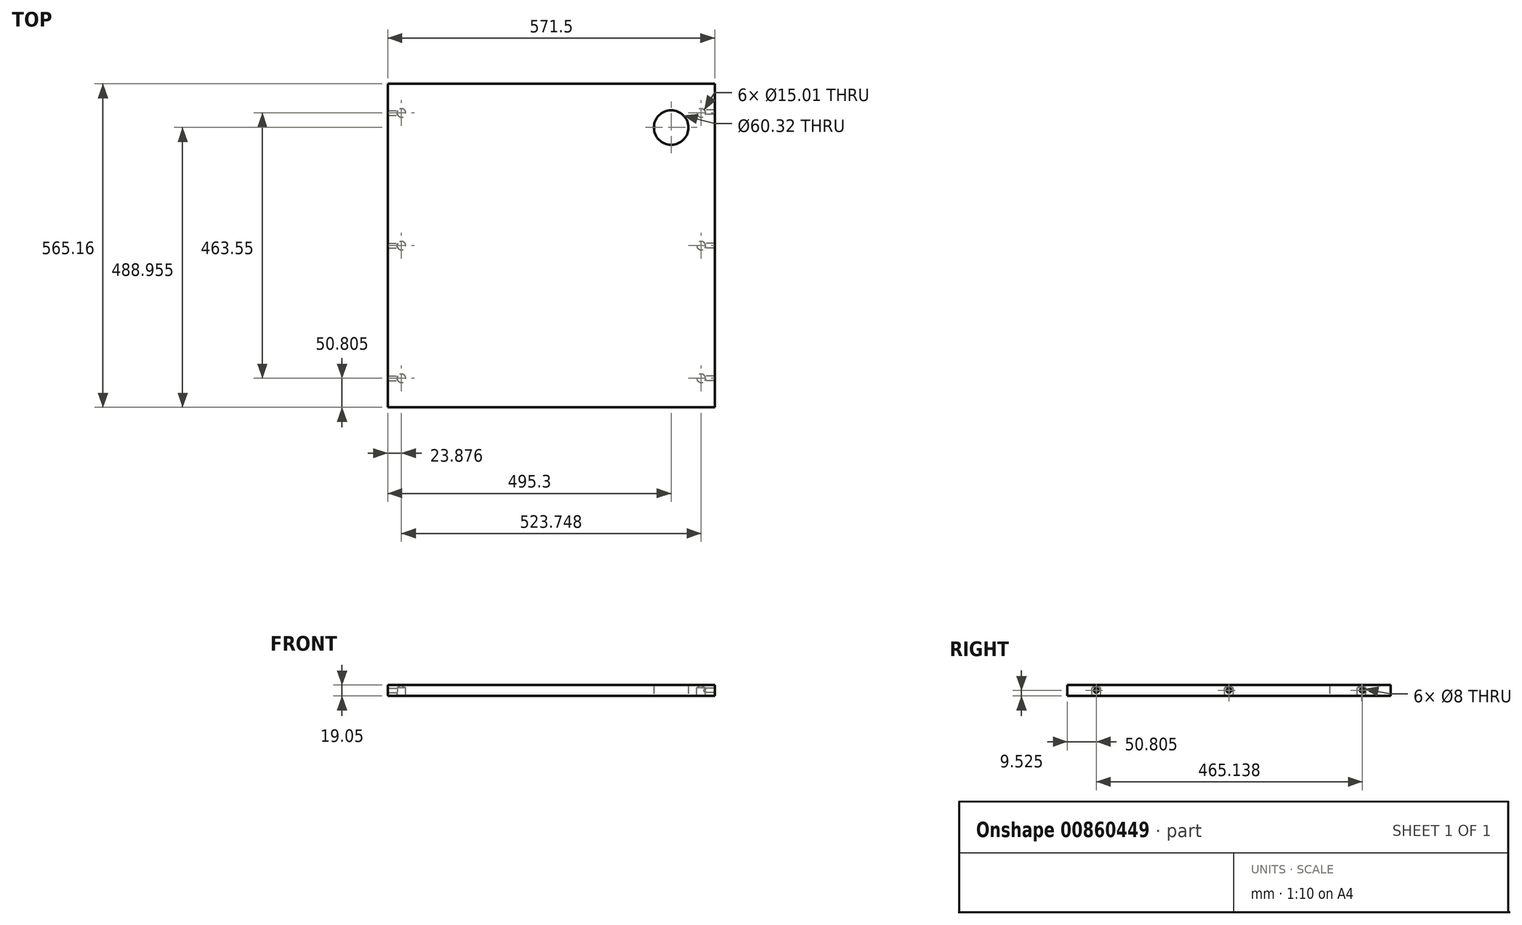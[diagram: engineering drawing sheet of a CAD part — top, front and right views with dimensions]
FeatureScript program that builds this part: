
annotation { "Feature Type Name" : "Feature", "Feature Type Description" : "" }
export const myFeature = defineFeature(function(context is Context, id is Id, definition is map)
    precondition{}
    {
        {
            var Q0;
            Q0=qCreatedBy(makeId("Top.planeOp"),FACE);
            var sketch = newSketch(context, id + "F0", { "sketchPlane" : qUnion([Q0])});
            skLineSegment(sketch, "E0.bottom", {"start": v(285.75, 282.58) * mm, "end": v(-285.75, 282.58) * mm});
            skLineSegment(sketch, "E0.top", {"start": v(285.75, -282.57) * mm, "end": v(-285.75, -282.58) * mm});
            skLineSegment(sketch, "E0.left", {"start": v(285.75, 282.58) * mm, "end": v(285.75, -282.58) * mm});
            skLineSegment(sketch, "E0.right", {"start": v(-285.75, 282.58) * mm, "end": v(-285.75, -282.58) * mm});
            skPoint(sketch, "E0.middle", {"position": v(0, 0) * mm});
            skCircle(sketch, "E1", {"center": v(209.55, 206.38) * mm, "radius": 30.16 * mm});
            skLineSegment(sketch, "E2", {"start": v(209.55, 206.38) * mm, "end": v(285.75, 206.38) * mm});
            skLineSegment(sketch, "E3", {"start": v(209.55, 206.38) * mm, "end": v(209.55, 282.58) * mm});
            skSolve(sketch);
        }
        {
            var Q0;
            Q0=makeQuery(id+"F0.imprint","IMPRINT",FACE,{"disambiguationData":[TD([[makeQuery(id+"F0.imprint","IMPRINT",EDGE,{"derivedFrom":sQuery(id+"F0.wireOp",EDGE,"E0.top")}),-1.0]])]});
            var Q1;
            {var subQ1=sQuery(id+"F0.wireOp",EDGE,"E0.left");var subQ7=sQuery(id+"F0.wireOp",EDGE,"E0.bottom");var subQ8=makeQuery(id+"F0.imprint","INTERSECT",VERTEX,{"derivedFrom":[subQ7,subQ1]});Q1=makeQuery(id+"F0.imprint","IMPRINT",FACE,{"disambiguationData":[TD([[makeQuery(id+"F0.imprint","IMPRINT",EDGE,{"disambiguationData":[TD([[subQ8,-1.0]])],"derivedFrom":subQ7}),1.0]])]});}
            extrude(context, id + "F1", {"entities" : qUnion([Q0, Q1]), "depth" : 19.05 * mm, "offsetDistance" : 25.4 * mm});
        }
        {
            var Q0;
            Q0=makeQuery(id+"F1.opExtrude","CAP_FACE",FACE,{"disambiguationData":[OSD([sQuery(id+"F0.wireOp",EDGE,"E0.bottom"),sQuery(id+"F0.wireOp",EDGE,"E0.top"),sQuery(id+"F0.wireOp",EDGE,"E0.left"),sQuery(id+"F0.wireOp",EDGE,"E0.right"),sQuery(id+"F0.wireOp",EDGE,"E1")])],"isStart":true});
            var sketch = newSketch(context, id + "F2", { "sketchPlane" : qUnion([Q0])});
            skLineSegment(sketch, "E4", {"start": v(-285.75, 282.58) * mm, "end": v(-261.87, 282.58) * mm});
            skLineSegment(sketch, "E5", {"start": v(-261.87, 282.58) * mm, "end": v(-261.87, 231.78) * mm});
            skLineSegment(sketch, "E6", {"start": v(-285.75, -282.57) * mm, "end": v(-261.87, -282.57) * mm});
            skLineSegment(sketch, "E7", {"start": v(-261.87, -282.57) * mm, "end": v(-261.87, -231.78) * mm});
            skLineSegment(sketch, "E8", {"start": v(-285.75, 0) * mm, "end": v(-261.87, 0) * mm});
            skLineSegment(sketch, "E9", {"start": v(285.75, 0) * mm, "end": v(261.87, 0) * mm});
            skLineSegment(sketch, "E10", {"start": v(285.75, 282.57) * mm, "end": v(261.87, 282.57) * mm});
            skLineSegment(sketch, "E11", {"start": v(261.87, 282.57) * mm, "end": v(261.87, 231.77) * mm});
            skLineSegment(sketch, "E12", {"start": v(285.75, -282.58) * mm, "end": v(261.87, -282.58) * mm});
            skLineSegment(sketch, "E13", {"start": v(261.87, -282.58) * mm, "end": v(261.87, -231.78) * mm});
            skPoint(sketch, "E14", {"position": v(-261.87, 231.78) * mm});
            skPoint(sketch, "E15", {"position": v(-261.87, 0) * mm});
            skPoint(sketch, "E16", {"position": v(-261.87, -231.78) * mm});
            skPoint(sketch, "E17", {"position": v(261.87, -231.78) * mm});
            skPoint(sketch, "E18", {"position": v(261.87, 0) * mm});
            skPoint(sketch, "E19", {"position": v(261.87, 231.77) * mm});
            skSolve(sketch);
        }
        {
            var Q0;
            Q0=sQuery(id+"F2.wireOp",VERTEX,"E14");
            var Q1;
            Q1=sQuery(id+"F2.wireOp",VERTEX,"E19");
            var Q2;
            Q2=sQuery(id+"F2.wireOp",VERTEX,"E15");
            var Q3;
            Q3=sQuery(id+"F2.wireOp",VERTEX,"E18");
            var Q4;
            Q4=sQuery(id+"F2.wireOp",VERTEX,"E17");
            var Q5;
            Q5=sQuery(id+"F2.wireOp",VERTEX,"E16");
            var Q6;
            Q6=makeQuery(id+"F1.opExtrude","SWEPT_BODY",BODY,{"disambiguationData":[OSD([sQuery(id+"F0.wireOp",EDGE,"E0.bottom"),sQuery(id+"F0.wireOp",EDGE,"E0.top"),sQuery(id+"F0.wireOp",EDGE,"E0.left"),sQuery(id+"F0.wireOp",EDGE,"E0.right"),sQuery(id+"F0.wireOp",EDGE,"E1")])]});
            hole(context, id + "F3", {"style" : HoleStyle.SIMPLE, "endStyle" : HoleEndStyle.BLIND, "holeDiameter" : 15 * mm, "majorDiameter" : 6.35 * mm, "holeDepth" : 14.22 * mm, "isTappedThrough" : true, "tappedDepth" : 12.7 * mm, "tapClearance" : 3, "locations" : qUnion([Q0, Q1, Q2, Q3, Q4, Q5]), "scope" : qUnion([Q6]), "startStyle" : HoleStartStyle.SKETCH});
        }
        {
            var Q0;
            Q0=makeQuery(id+"F1.opExtrude","SWEPT_FACE",FACE,{"disambiguationData":[OSD([sQuery(id+"F0.wireOp",EDGE,"E0.left")])]});
            var sketch = newSketch(context, id + "F4", { "sketchPlane" : qUnion([Q0])});
            skPoint(sketch, "E20", {"position": v(0, 9.52) * mm});
            skPoint(sketch, "E20.positionSnap0", {"position": v(0, 19.05) * mm});
            skPoint(sketch, "E21", {"position": v(-231.77, 9.53) * mm});
            skPoint(sketch, "E22", {"position": v(233.36, 9.52) * mm});
            skLineSegment(sketch, "E23", {"start": v(-231.77, 9.53) * mm, "end": v(-231.77, 0) * mm});
            skLineSegment(sketch, "E24", {"start": v(-231.77, 0) * mm, "end": v(-282.57, 0) * mm});
            skLineSegment(sketch, "E25", {"start": v(0, 0) * mm, "end": v(0, 9.53) * mm});
            skPoint(sketch, "E26", {"position": v(0, 9.53) * mm});
            skLineSegment(sketch, "E27", {"start": v(233.36, 9.52) * mm, "end": v(233.36, 0) * mm});
            skSolve(sketch);
        }
        {
            var Q0;
            Q0=sQuery(id+"F4.wireOp",VERTEX,"E21");
            var Q1;
            Q1=sQuery(id+"F4.wireOp",VERTEX,"E20");
            var Q2;
            Q2=sQuery(id+"F4.wireOp",VERTEX,"E22");
            var Q3;
            Q3=makeQuery(id+"F1.opExtrude","SWEPT_BODY",BODY,{"disambiguationData":[OSD([sQuery(id+"F0.wireOp",EDGE,"E0.bottom"),sQuery(id+"F0.wireOp",EDGE,"E0.top"),sQuery(id+"F0.wireOp",EDGE,"E0.left"),sQuery(id+"F0.wireOp",EDGE,"E0.right"),sQuery(id+"F0.wireOp",EDGE,"E1")])]});
            hole(context, id + "F5", {"style" : HoleStyle.SIMPLE, "endStyle" : HoleEndStyle.BLIND, "holeDiameter" : 8 * mm, "majorDiameter" : 6.35 * mm, "holeDepth" : 25.4 * mm, "isTappedThrough" : true, "tappedDepth" : 12.7 * mm, "tapClearance" : 3, "locations" : qUnion([Q0, Q1, Q2]), "scope" : qUnion([Q3]), "startStyle" : HoleStartStyle.SKETCH});
        }
        {
            var Q0;
            Q0=makeQuery(id+"F1.opExtrude","SWEPT_FACE",FACE,{"disambiguationData":[OSD([sQuery(id+"F0.wireOp",EDGE,"E0.right")])]});
            var sketch = newSketch(context, id + "F6", { "sketchPlane" : qUnion([Q0])});
            skPoint(sketch, "E28", {"position": v(-231.77, 9.53) * mm});
            skPoint(sketch, "E29", {"position": v(231.78, 9.53) * mm});
            skLineSegment(sketch, "E30", {"start": v(0, 0) * mm, "end": v(0, 9.53) * mm});
            skPoint(sketch, "E31", {"position": v(0, 9.53) * mm});
            skLineSegment(sketch, "E32", {"start": v(-231.77, 9.53) * mm, "end": v(-231.77, 0) * mm});
            skLineSegment(sketch, "E33", {"start": v(-231.77, 0) * mm, "end": v(-282.57, 0) * mm});
            skLineSegment(sketch, "E34", {"start": v(231.78, 9.53) * mm, "end": v(231.78, 0) * mm});
            skLineSegment(sketch, "E35", {"start": v(231.78, 0) * mm, "end": v(282.58, 0) * mm});
            skSolve(sketch);
        }
        {
            var Q0;
            Q0=sQuery(id+"F6.wireOp",VERTEX,"7JFDCdo1-Y3dr-wsHc-LP2G-7qkS5dpKQL4z.end");
            var Q1;
            Q1=sQuery(id+"F6.wireOp",VERTEX,"E31");
            var Q2;
            Q2=sQuery(id+"F6.wireOp",VERTEX,"E29");
            var Q3;
            Q3=sQuery(id+"F6.wireOp",VERTEX,"E28");
            var Q4;
            Q4=makeQuery(id+"F1.opExtrude","SWEPT_BODY",BODY,{"disambiguationData":[OSD([sQuery(id+"F0.wireOp",EDGE,"E0.bottom"),sQuery(id+"F0.wireOp",EDGE,"E0.top"),sQuery(id+"F0.wireOp",EDGE,"E0.left"),sQuery(id+"F0.wireOp",EDGE,"E0.right"),sQuery(id+"F0.wireOp",EDGE,"E1")])]});
            hole(context, id + "F7", {"style" : HoleStyle.SIMPLE, "endStyle" : HoleEndStyle.BLIND, "holeDiameter" : 8 * mm, "majorDiameter" : 6.35 * mm, "holeDepth" : 25.4 * mm, "isTappedThrough" : true, "tappedDepth" : 12.7 * mm, "tapClearance" : 3, "locations" : qUnion([Q0, Q1, Q2, Q3]), "scope" : qUnion([Q4]), "startStyle" : HoleStartStyle.SKETCH});
        }
    });
